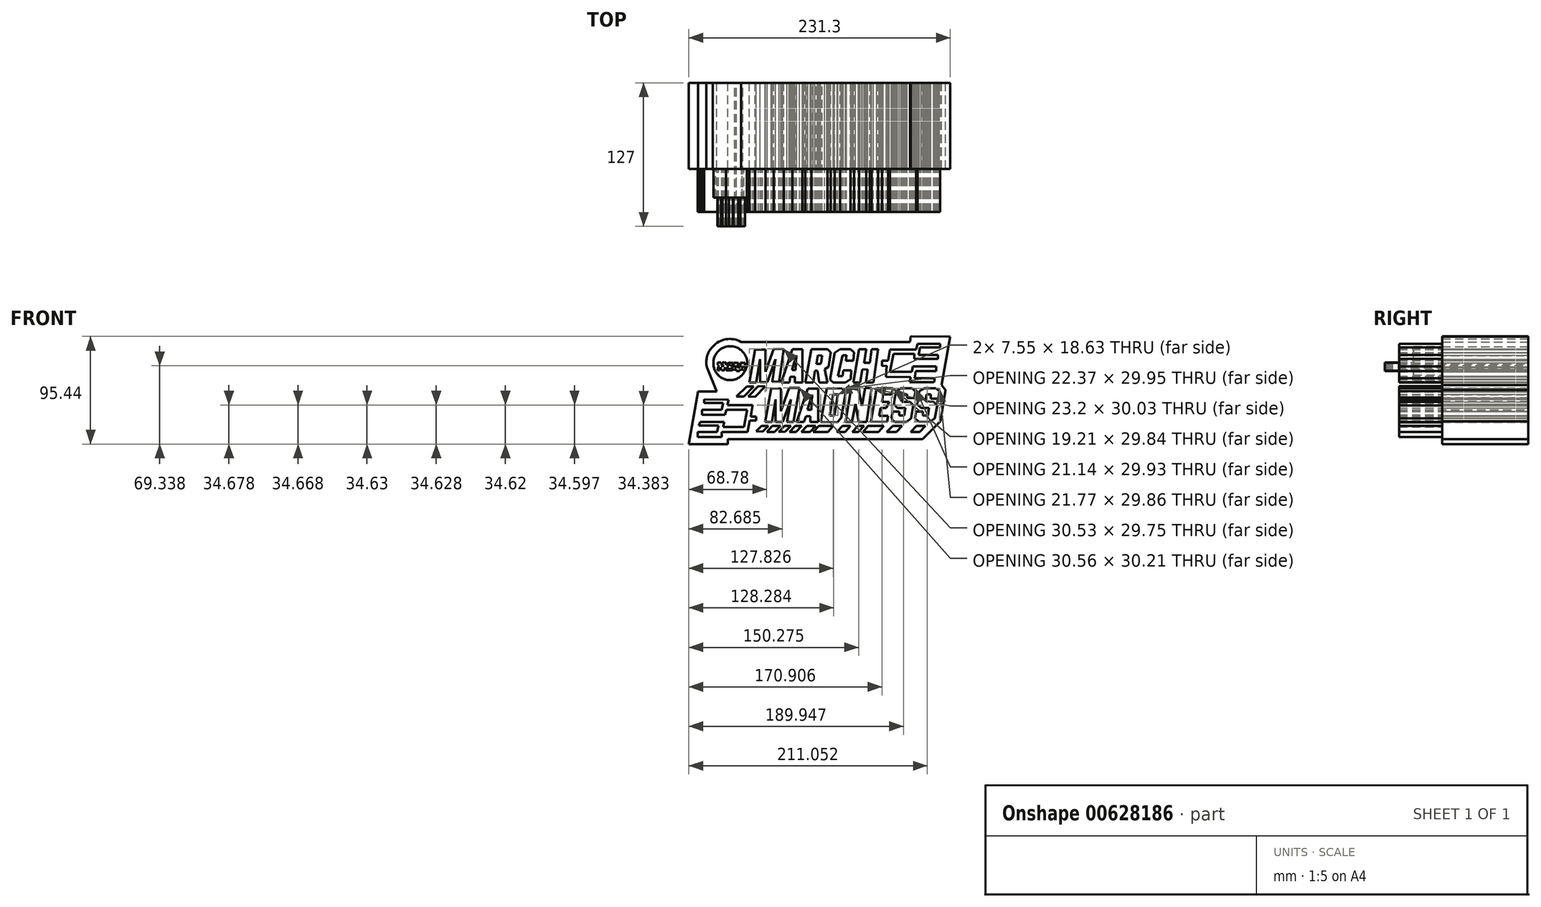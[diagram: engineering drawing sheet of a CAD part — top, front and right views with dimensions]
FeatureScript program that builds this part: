
annotation { "Feature Type Name" : "Feature", "Feature Type Description" : "" }
export const myFeature = defineFeature(function(context is Context, id is Id, definition is map)
    precondition{}
    {
        {
            var Q0;
            Q0=qCreatedBy(makeId("Front.planeOp"),FACE);
            var sketch = newSketch(context, id + "F0", { "sketchPlane" : qUnion([Q0])});
            skLineSegment(sketch, "E0", {"start": v(-36.13, -12.76) * mm, "end": v(-36.13, -15.94) * mm});
            skLineSegment(sketch, "E1", {"start": v(-36.13, -15.94) * mm, "end": v(-19.37, -15.94) * mm});
            skLineSegment(sketch, "E2", {"start": v(-19.37, -15.94) * mm, "end": v(-20.47, -21.93) * mm});
            skLineSegment(sketch, "E3", {"start": v(-20.47, -21.93) * mm, "end": v(-37.96, -21.93) * mm});
            skLineSegment(sketch, "E4", {"start": v(-37.96, -21.93) * mm, "end": v(-37.96, -26.21) * mm});
            skLineSegment(sketch, "E5", {"start": v(-37.96, -26.21) * mm, "end": v(-17.66, -26.21) * mm});
            skLineSegment(sketch, "E6", {"start": v(-17.66, -26.21) * mm, "end": v(-16.56, -21.93) * mm});
            skLineSegment(sketch, "E7", {"start": v(-16.56, -21.93) * mm, "end": v(1.79, -21.93) * mm});
            skLineSegment(sketch, "E8", {"start": v(1.79, -21.93) * mm, "end": v(-1.03, -37.22) * mm});
            skLineSegment(sketch, "E9", {"start": v(-1.03, -37.22) * mm, "end": v(-19.37, -37.22) * mm});
            skLineSegment(sketch, "E10", {"start": v(-19.37, -37.22) * mm, "end": v(-18.4, -32.82) * mm});
            skLineSegment(sketch, "E11", {"start": v(-18.4, -32.82) * mm, "end": v(-39.8, -32.82) * mm});
            skLineSegment(sketch, "E12", {"start": v(-39.8, -32.82) * mm, "end": v(-40.9, -35.88) * mm});
            skLineSegment(sketch, "E13", {"start": v(-40.9, -35.88) * mm, "end": v(-23.53, -35.88) * mm});
            skLineSegment(sketch, "E14", {"start": v(-23.53, -35.88) * mm, "end": v(-24.63, -41.62) * mm});
            skLineSegment(sketch, "E15", {"start": v(-24.63, -41.62) * mm, "end": v(-41.88, -41.62) * mm});
            skLineSegment(sketch, "E16", {"start": v(-41.88, -41.62) * mm, "end": v(-41.88, -46.15) * mm});
            skLineSegment(sketch, "E17", {"start": v(-41.88, -46.15) * mm, "end": v(-20.47, -46.15) * mm});
            skLineSegment(sketch, "E18", {"start": v(-20.47, -46.15) * mm, "end": v(-20.47, -41.62) * mm});
            skLineSegment(sketch, "E19", {"start": v(-20.47, -41.62) * mm, "end": v(2.15, -41.62) * mm});
            skLineSegment(sketch, "E20", {"start": v(2.15, -41.62) * mm, "end": v(4.23, -31.6) * mm});
            skLineSegment(sketch, "E21", {"start": v(4.23, -31.6) * mm, "end": v(9.98, -31.6) * mm});
            skLineSegment(sketch, "E22", {"start": v(9.98, -31.6) * mm, "end": v(9.98, -27.93) * mm});
            skLineSegment(sketch, "E23", {"start": v(9.98, -27.93) * mm, "end": v(5.21, -27.93) * mm});
            skLineSegment(sketch, "E24", {"start": v(5.21, -27.93) * mm, "end": v(6.68, -17.65) * mm});
            skLineSegment(sketch, "E25", {"start": v(6.68, -17.65) * mm, "end": v(-15.46, -17.65) * mm});
            skLineSegment(sketch, "E26", {"start": v(-15.46, -17.65) * mm, "end": v(-14.6, -12.88) * mm});
            skLineSegment(sketch, "E27", {"start": v(-14.6, -12.88) * mm, "end": v(-36.13, -12.76) * mm});
            skLineSegment(sketch, "E28", {"start": v(-7.5, -10.31) * mm, "end": v(1.54, -1.26) * mm});
            skLineSegment(sketch, "E29", {"start": v(1.54, -1.26) * mm, "end": v(7.54, -1.3) * mm});
            skLineSegment(sketch, "E30", {"start": v(7.54, -1.3) * mm, "end": v(-1.03, -10.31) * mm});
            skLineSegment(sketch, "E31", {"start": v(-1.03, -10.31) * mm, "end": v(-7.5, -10.31) * mm});
            skLineSegment(sketch, "E32", {"start": v(11.82, -0.9) * mm, "end": v(2.87, -10.31) * mm});
            skLineSegment(sketch, "E33", {"start": v(2.87, -10.31) * mm, "end": v(9, -10.35) * mm});
            skLineSegment(sketch, "E34", {"start": v(9, -10.35) * mm, "end": v(17.7, -1.19) * mm});
            skLineSegment(sketch, "E35", {"start": v(17.7, -1.19) * mm, "end": v(11.82, -0.9) * mm});
            skLineSegment(sketch, "E36", {"start": v(17.7, -32.82) * mm, "end": v(23.07, -2.98) * mm});
            skLineSegment(sketch, "E37", {"start": v(23.07, -2.98) * mm, "end": v(31.63, -3.02) * mm});
            skLineSegment(sketch, "E38", {"start": v(31.63, -3.02) * mm, "end": v(31.63, -23.16) * mm});
            skLineSegment(sketch, "E39", {"start": v(31.63, -23.16) * mm, "end": v(39.1, -2.6) * mm});
            skLineSegment(sketch, "E40", {"start": v(39.1, -2.6) * mm, "end": v(48.26, -2.66) * mm});
            skLineSegment(sketch, "E41", {"start": v(48.26, -2.66) * mm, "end": v(42.88, -32.82) * mm});
            skLineSegment(sketch, "E42", {"start": v(42.88, -32.82) * mm, "end": v(37.13, -32.79) * mm});
            skLineSegment(sketch, "E43", {"start": v(37.13, -32.79) * mm, "end": v(40.68, -12.76) * mm});
            skLineSegment(sketch, "E44", {"start": v(40.68, -12.76) * mm, "end": v(33.46, -32.82) * mm});
            skLineSegment(sketch, "E45", {"start": v(33.46, -32.82) * mm, "end": v(26.98, -32.78) * mm});
            skLineSegment(sketch, "E46", {"start": v(26.98, -32.78) * mm, "end": v(26.98, -12.76) * mm});
            skLineSegment(sketch, "E47", {"start": v(26.98, -12.76) * mm, "end": v(23.68, -32.82) * mm});
            skLineSegment(sketch, "E48", {"start": v(23.68, -32.82) * mm, "end": v(17.7, -32.82) * mm});
            skLineSegment(sketch, "E49", {"start": v(45.7, -32.82) * mm, "end": v(52.18, -32.85) * mm});
            skLineSegment(sketch, "E50", {"start": v(52.18, -32.85) * mm, "end": v(54.07, -27.6) * mm});
            skLineSegment(sketch, "E51", {"start": v(54.07, -27.6) * mm, "end": v(57.92, -27.62) * mm});
            skLineSegment(sketch, "E52", {"start": v(57.92, -27.62) * mm, "end": v(57.92, -32.82) * mm});
            skLineSegment(sketch, "E53", {"start": v(57.92, -32.82) * mm, "end": v(64.69, -32.86) * mm});
            skLineSegment(sketch, "E54", {"start": v(64.69, -32.86) * mm, "end": v(64.86, -3.13) * mm});
            skLineSegment(sketch, "E55", {"start": v(64.86, -3.13) * mm, "end": v(55.52, -3.08) * mm});
            skLineSegment(sketch, "E56", {"start": v(55.52, -3.08) * mm, "end": v(45.7, -32.82) * mm});
            skLineSegment(sketch, "E57", {"start": v(55.23, -21.93) * mm, "end": v(58.65, -21.95) * mm});
            skLineSegment(sketch, "E58", {"start": v(58.65, -21.95) * mm, "end": v(59.31, -8.43) * mm});
            skLineSegment(sketch, "E59", {"start": v(59.31, -8.43) * mm, "end": v(55.23, -21.93) * mm});
            skLineSegment(sketch, "E60", {"start": v(66.94, -32.82) * mm, "end": v(81.48, -32.9) * mm});
            skLineSegment(sketch, "E61", {"start": v(81.48, -32.9) * mm, "end": v(85.13, -29.25) * mm});
            skLineSegment(sketch, "E62", {"start": v(85.13, -29.25) * mm, "end": v(89.31, -6) * mm});
            skLineSegment(sketch, "E63", {"start": v(89.31, -6) * mm, "end": v(86.19, -3.03) * mm});
            skLineSegment(sketch, "E64", {"start": v(86.19, -3.03) * mm, "end": v(72.4, -2.95) * mm});
            skLineSegment(sketch, "E65", {"start": v(72.4, -2.95) * mm, "end": v(66.94, -32.82) * mm});
            skLineSegment(sketch, "E66", {"start": v(78.14, -8.37) * mm, "end": v(74.8, -26.92) * mm});
            skLineSegment(sketch, "E67", {"start": v(74.8, -26.92) * mm, "end": v(79.01, -26.95) * mm});
            skLineSegment(sketch, "E68", {"start": v(79.01, -26.95) * mm, "end": v(82.36, -8.32) * mm});
            skLineSegment(sketch, "E69", {"start": v(82.36, -8.32) * mm, "end": v(78.14, -8.37) * mm});
            skLineSegment(sketch, "E70", {"start": v(94.07, -2.77) * mm, "end": v(88.98, -32.59) * mm});
            skLineSegment(sketch, "E71", {"start": v(88.98, -32.59) * mm, "end": v(94.58, -32.62) * mm});
            skLineSegment(sketch, "E72", {"start": v(94.58, -32.62) * mm, "end": v(97.92, -16.88) * mm});
            skLineSegment(sketch, "E73", {"start": v(97.92, -16.88) * mm, "end": v(100.76, -32.66) * mm});
            skLineSegment(sketch, "E74", {"start": v(100.76, -32.66) * mm, "end": v(107.52, -32.7) * mm});
            skLineSegment(sketch, "E75", {"start": v(107.52, -32.7) * mm, "end": v(112.17, -2.7) * mm});
            skLineSegment(sketch, "E76", {"start": v(112.17, -2.7) * mm, "end": v(106.43, -2.67) * mm});
            skLineSegment(sketch, "E77", {"start": v(106.43, -2.67) * mm, "end": v(103.67, -18.4) * mm});
            skLineSegment(sketch, "E78", {"start": v(103.67, -18.4) * mm, "end": v(100.4, -2.99) * mm});
            skLineSegment(sketch, "E79", {"start": v(100.4, -2.99) * mm, "end": v(94.07, -2.77) * mm});
            skLineSegment(sketch, "E80", {"start": v(116.68, -2.77) * mm, "end": v(111.6, -32.53) * mm});
            skLineSegment(sketch, "E81", {"start": v(111.6, -32.53) * mm, "end": v(125.7, -32.61) * mm});
            skLineSegment(sketch, "E82", {"start": v(125.7, -32.61) * mm, "end": v(126.6, -27.3) * mm});
            skLineSegment(sketch, "E83", {"start": v(126.6, -27.3) * mm, "end": v(118.86, -27.26) * mm});
            skLineSegment(sketch, "E84", {"start": v(118.86, -27.26) * mm, "end": v(120.06, -20.24) * mm});
            skLineSegment(sketch, "E85", {"start": v(120.06, -20.24) * mm, "end": v(125.26, -20.27) * mm});
            skLineSegment(sketch, "E86", {"start": v(125.26, -20.27) * mm, "end": v(127.52, -14.99) * mm});
            skLineSegment(sketch, "E87", {"start": v(127.52, -14.99) * mm, "end": v(121.26, -14.95) * mm});
            skLineSegment(sketch, "E88", {"start": v(121.26, -14.95) * mm, "end": v(122.39, -8.37) * mm});
            skLineSegment(sketch, "E89", {"start": v(122.39, -8.37) * mm, "end": v(129.85, -8.41) * mm});
            skLineSegment(sketch, "E90", {"start": v(129.85, -8.41) * mm, "end": v(130.8, -2.77) * mm});
            skLineSegment(sketch, "E91", {"start": v(130.8, -2.77) * mm, "end": v(116.68, -2.77) * mm});
            skLineSegment(sketch, "E92", {"start": v(133.63, -5.53) * mm, "end": v(131.7, -16.82) * mm});
            skLineSegment(sketch, "E93", {"start": v(131.7, -16.82) * mm, "end": v(134.8, -20.22) * mm});
            skLineSegment(sketch, "E94", {"start": v(134.8, -20.22) * mm, "end": v(142.06, -20.27) * mm});
            skLineSegment(sketch, "E95", {"start": v(142.06, -20.27) * mm, "end": v(140.9, -27.12) * mm});
            skLineSegment(sketch, "E96", {"start": v(140.9, -27.12) * mm, "end": v(136.54, -27.1) * mm});
            skLineSegment(sketch, "E97", {"start": v(136.54, -27.1) * mm, "end": v(136.54, -23.57) * mm});
            skLineSegment(sketch, "E98", {"start": v(136.54, -23.57) * mm, "end": v(130.72, -23.54) * mm});
            skLineSegment(sketch, "E99", {"start": v(130.72, -23.54) * mm, "end": v(129.68, -29.63) * mm});
            skLineSegment(sketch, "E100", {"start": v(129.68, -29.63) * mm, "end": v(132.4, -32.59) * mm});
            skLineSegment(sketch, "E101", {"start": v(132.4, -32.59) * mm, "end": v(142.8, -32.65) * mm});
            skLineSegment(sketch, "E102", {"start": v(142.8, -32.65) * mm, "end": v(146.94, -29.39) * mm});
            skLineSegment(sketch, "E103", {"start": v(146.94, -29.39) * mm, "end": v(148.89, -17.94) * mm});
            skLineSegment(sketch, "E104", {"start": v(148.89, -17.94) * mm, "end": v(146.06, -14.84) * mm});
            skLineSegment(sketch, "E105", {"start": v(146.06, -14.84) * mm, "end": v(138.8, -14.8) * mm});
            skLineSegment(sketch, "E106", {"start": v(138.8, -14.8) * mm, "end": v(139.89, -8.37) * mm});
            skLineSegment(sketch, "E107", {"start": v(139.89, -8.37) * mm, "end": v(143.66, -8.4) * mm});
            skLineSegment(sketch, "E108", {"start": v(143.66, -8.4) * mm, "end": v(143.66, -11.5) * mm});
            skLineSegment(sketch, "E109", {"start": v(143.66, -11.5) * mm, "end": v(149.84, -11.53) * mm});
            skLineSegment(sketch, "E110", {"start": v(149.84, -11.53) * mm, "end": v(150.82, -5.84) * mm});
            skLineSegment(sketch, "E111", {"start": v(150.82, -5.84) * mm, "end": v(147.88, -2.77) * mm});
            skLineSegment(sketch, "E112", {"start": v(147.88, -2.77) * mm, "end": v(138, -2.71) * mm});
            skLineSegment(sketch, "E113", {"start": v(138, -2.71) * mm, "end": v(133.63, -5.53) * mm});
            skLineSegment(sketch, "E114", {"start": v(159.8, -14.33) * mm, "end": v(160.83, -8.37) * mm});
            skLineSegment(sketch, "E115", {"start": v(160.83, -8.37) * mm, "end": v(164.53, -8.4) * mm});
            skLineSegment(sketch, "E116", {"start": v(164.53, -8.4) * mm, "end": v(164.53, -11.93) * mm});
            skLineSegment(sketch, "E117", {"start": v(164.53, -11.93) * mm, "end": v(170.13, -11.97) * mm});
            skLineSegment(sketch, "E118", {"start": v(170.13, -11.97) * mm, "end": v(171.26, -11.24) * mm});
            skLineSegment(sketch, "E119", {"start": v(171.26, -11.24) * mm, "end": v(172.24, -5.53) * mm});
            skLineSegment(sketch, "E120", {"start": v(172.24, -5.53) * mm, "end": v(168.97, -2.77) * mm});
            skLineSegment(sketch, "E121", {"start": v(168.97, -2.77) * mm, "end": v(158.72, -2.71) * mm});
            skLineSegment(sketch, "E122", {"start": v(158.72, -2.71) * mm, "end": v(154.35, -5.53) * mm});
            skLineSegment(sketch, "E123", {"start": v(154.35, -5.53) * mm, "end": v(152.35, -17.26) * mm});
            skLineSegment(sketch, "E124", {"start": v(152.35, -17.26) * mm, "end": v(155.8, -20.22) * mm});
            skLineSegment(sketch, "E125", {"start": v(155.8, -20.22) * mm, "end": v(162.93, -20.26) * mm});
            skLineSegment(sketch, "E126", {"start": v(162.93, -20.26) * mm, "end": v(161.79, -26.99) * mm});
            skLineSegment(sketch, "E127", {"start": v(161.79, -26.99) * mm, "end": v(157.55, -26.97) * mm});
            skLineSegment(sketch, "E128", {"start": v(157.55, -26.97) * mm, "end": v(157.55, -23.57) * mm});
            skLineSegment(sketch, "E129", {"start": v(157.55, -23.57) * mm, "end": v(151.52, -23.53) * mm});
            skLineSegment(sketch, "E130", {"start": v(151.52, -23.53) * mm, "end": v(150.47, -29.67) * mm});
            skLineSegment(sketch, "E131", {"start": v(150.47, -29.67) * mm, "end": v(153.55, -32.51) * mm});
            skLineSegment(sketch, "E132", {"start": v(153.55, -32.51) * mm, "end": v(163.59, -32.57) * mm});
            skLineSegment(sketch, "E133", {"start": v(163.59, -32.57) * mm, "end": v(168.1, -29.65) * mm});
            skLineSegment(sketch, "E134", {"start": v(168.1, -29.65) * mm, "end": v(170.1, -18.02) * mm});
            skLineSegment(sketch, "E135", {"start": v(170.1, -18.02) * mm, "end": v(167, -14.84) * mm});
            skLineSegment(sketch, "E136", {"start": v(167, -14.84) * mm, "end": v(159.8, -14.33) * mm});
            skLineSegment(sketch, "E137", {"start": v(14.47, -36.25) * mm, "end": v(9.76, -41.02) * mm});
            skLineSegment(sketch, "E138", {"start": v(9.76, -41.02) * mm, "end": v(15.57, -41.44) * mm});
            skLineSegment(sketch, "E139", {"start": v(15.57, -41.44) * mm, "end": v(20.7, -36.25) * mm});
            skLineSegment(sketch, "E140", {"start": v(20.7, -36.25) * mm, "end": v(14.47, -36.25) * mm});
            skLineSegment(sketch, "E141", {"start": v(24.19, -36.25) * mm, "end": v(19.3, -41.45) * mm});
            skLineSegment(sketch, "E142", {"start": v(19.3, -41.45) * mm, "end": v(26.08, -41.5) * mm});
            skLineSegment(sketch, "E143", {"start": v(26.08, -41.5) * mm, "end": v(31.34, -36.25) * mm});
            skLineSegment(sketch, "E144", {"start": v(31.34, -36.25) * mm, "end": v(24.19, -36.25) * mm});
            skLineSegment(sketch, "E145", {"start": v(29.94, -41.45) * mm, "end": v(34.83, -36.25) * mm});
            skLineSegment(sketch, "E146", {"start": v(34.83, -36.25) * mm, "end": v(40.64, -36.29) * mm});
            skLineSegment(sketch, "E147", {"start": v(40.64, -36.29) * mm, "end": v(35.56, -41.4) * mm});
            skLineSegment(sketch, "E148", {"start": v(35.56, -41.4) * mm, "end": v(29.94, -41.45) * mm});
            skLineSegment(sketch, "E149", {"start": v(39.23, -41.45) * mm, "end": v(44.3, -36.25) * mm});
            skLineSegment(sketch, "E150", {"start": v(44.3, -36.25) * mm, "end": v(50.24, -36.29) * mm});
            skLineSegment(sketch, "E151", {"start": v(50.24, -36.29) * mm, "end": v(45.22, -41.45) * mm});
            skLineSegment(sketch, "E152", {"start": v(45.22, -41.45) * mm, "end": v(39.23, -41.45) * mm});
            skLineSegment(sketch, "E153", {"start": v(49.75, -41.45) * mm, "end": v(55, -36.25) * mm});
            skLineSegment(sketch, "E154", {"start": v(55, -36.25) * mm, "end": v(62.6, -36.3) * mm});
            skLineSegment(sketch, "E155", {"start": v(62.6, -36.3) * mm, "end": v(57.58, -41.45) * mm});
            skLineSegment(sketch, "E156", {"start": v(57.58, -41.45) * mm, "end": v(49.75, -41.45) * mm});
            skLineSegment(sketch, "E157", {"start": v(60.51, -41.45) * mm, "end": v(65.47, -36.25) * mm});
            skLineSegment(sketch, "E158", {"start": v(65.47, -36.25) * mm, "end": v(78.14, -36.33) * mm});
            skLineSegment(sketch, "E159", {"start": v(78.14, -36.33) * mm, "end": v(73.48, -41.45) * mm});
            skLineSegment(sketch, "E160", {"start": v(73.48, -41.45) * mm, "end": v(60.51, -41.45) * mm});
            skLineSegment(sketch, "E161", {"start": v(81.3, -41.45) * mm, "end": v(86.5, -36.25) * mm});
            skLineSegment(sketch, "E162", {"start": v(86.5, -36.25) * mm, "end": v(93.47, -36.3) * mm});
            skLineSegment(sketch, "E163", {"start": v(93.47, -36.3) * mm, "end": v(88.46, -41.45) * mm});
            skLineSegment(sketch, "E164", {"start": v(88.46, -41.45) * mm, "end": v(81.3, -41.45) * mm});
            skLineSegment(sketch, "E165", {"start": v(94.82, -41.45) * mm, "end": v(99.96, -36.25) * mm});
            skLineSegment(sketch, "E166", {"start": v(99.96, -36.25) * mm, "end": v(105.46, -36.25) * mm});
            skLineSegment(sketch, "E167", {"start": v(105.46, -36.25) * mm, "end": v(100.45, -41.45) * mm});
            skLineSegment(sketch, "E168", {"start": v(100.45, -41.45) * mm, "end": v(94.82, -41.45) * mm});
            skLineSegment(sketch, "E169", {"start": v(104.48, -41.45) * mm, "end": v(109.07, -36.25) * mm});
            skLineSegment(sketch, "E170", {"start": v(109.07, -36.25) * mm, "end": v(123, -36.33) * mm});
            skLineSegment(sketch, "E171", {"start": v(123, -36.33) * mm, "end": v(118.18, -41.45) * mm});
            skLineSegment(sketch, "E172", {"start": v(118.18, -41.45) * mm, "end": v(104.48, -41.45) * mm});
            skLineSegment(sketch, "E173", {"start": v(125.46, -41.45) * mm, "end": v(130.72, -36.25) * mm});
            skLineSegment(sketch, "E174", {"start": v(130.72, -36.25) * mm, "end": v(139.1, -36.3) * mm});
            skLineSegment(sketch, "E175", {"start": v(139.1, -36.3) * mm, "end": v(134.14, -41.45) * mm});
            skLineSegment(sketch, "E176", {"start": v(134.14, -41.45) * mm, "end": v(125.46, -41.45) * mm});
            skLineSegment(sketch, "E177", {"start": v(146.74, -41.45) * mm, "end": v(151.7, -36.25) * mm});
            skLineSegment(sketch, "E178", {"start": v(151.7, -36.25) * mm, "end": v(159.8, -36.3) * mm});
            skLineSegment(sketch, "E179", {"start": v(159.8, -36.3) * mm, "end": v(154.75, -41.45) * mm});
            skLineSegment(sketch, "E180", {"start": v(154.75, -41.45) * mm, "end": v(146.74, -41.45) * mm});
            skLineSegment(sketch, "E181", {"start": v(3.82, 2.17) * mm, "end": v(9, 31.46) * mm});
            skLineSegment(sketch, "E182", {"start": v(9, 31.46) * mm, "end": v(18.26, 31.4) * mm});
            skLineSegment(sketch, "E183", {"start": v(18.26, 31.4) * mm, "end": v(18.17, 11.77) * mm});
            skLineSegment(sketch, "E184", {"start": v(18.17, 11.77) * mm, "end": v(25.48, 31.9) * mm});
            skLineSegment(sketch, "E185", {"start": v(25.48, 31.9) * mm, "end": v(34.34, 31.85) * mm});
            skLineSegment(sketch, "E186", {"start": v(34.34, 31.85) * mm, "end": v(30.18, 2.7) * mm});
            skLineSegment(sketch, "E187", {"start": v(30.18, 2.7) * mm, "end": v(24.19, 2.74) * mm});
            skLineSegment(sketch, "E188", {"start": v(24.19, 2.74) * mm, "end": v(27.04, 22.7) * mm});
            skLineSegment(sketch, "E189", {"start": v(27.04, 22.7) * mm, "end": v(19.74, 2.6) * mm});
            skLineSegment(sketch, "E190", {"start": v(19.74, 2.6) * mm, "end": v(13.5, 2.64) * mm});
            skLineSegment(sketch, "E191", {"start": v(13.5, 2.64) * mm, "end": v(13.5, 22.75) * mm});
            skLineSegment(sketch, "E192", {"start": v(13.5, 22.75) * mm, "end": v(9.98, 2.15) * mm});
            skLineSegment(sketch, "E193", {"start": v(9.98, 2.15) * mm, "end": v(3.82, 2.17) * mm});
            skLineSegment(sketch, "E194", {"start": v(32.1, 2.17) * mm, "end": v(41.78, 31.75) * mm});
            skLineSegment(sketch, "E195", {"start": v(41.78, 31.75) * mm, "end": v(50.69, 31.7) * mm});
            skLineSegment(sketch, "E196", {"start": v(50.69, 31.7) * mm, "end": v(50.69, 2.17) * mm});
            skLineSegment(sketch, "E197", {"start": v(50.69, 2.17) * mm, "end": v(44.29, 2.2) * mm});
            skLineSegment(sketch, "E198", {"start": v(44.29, 2.2) * mm, "end": v(44.29, 7.27) * mm});
            skLineSegment(sketch, "E199", {"start": v(44.29, 7.27) * mm, "end": v(40.14, 7.3) * mm});
            skLineSegment(sketch, "E200", {"start": v(40.14, 7.3) * mm, "end": v(39.26, 2.17) * mm});
            skLineSegment(sketch, "E201", {"start": v(39.26, 2.17) * mm, "end": v(32.1, 2.17) * mm});
            skLineSegment(sketch, "E202", {"start": v(53.37, 2.17) * mm, "end": v(58.6, 31.7) * mm});
            skLineSegment(sketch, "E203", {"start": v(58.6, 31.7) * mm, "end": v(72.91, 31.62) * mm});
            skLineSegment(sketch, "E204", {"start": v(72.91, 31.62) * mm, "end": v(75.82, 28.86) * mm});
            skLineSegment(sketch, "E205", {"start": v(75.82, 28.86) * mm, "end": v(74.02, 16.32) * mm});
            skLineSegment(sketch, "E206", {"start": v(74.02, 16.32) * mm, "end": v(70.56, 14.08) * mm});
            skLineSegment(sketch, "E207", {"start": v(70.56, 14.08) * mm, "end": v(72.92, 2.17) * mm});
            skLineSegment(sketch, "E208", {"start": v(72.92, 2.17) * mm, "end": v(65.74, 2.21) * mm});
            skLineSegment(sketch, "E209", {"start": v(65.74, 2.21) * mm, "end": v(64.18, 12.55) * mm});
            skLineSegment(sketch, "E210", {"start": v(64.18, 12.55) * mm, "end": v(61.85, 12.56) * mm});
            skLineSegment(sketch, "E211", {"start": v(61.85, 12.56) * mm, "end": v(60.36, 2.17) * mm});
            skLineSegment(sketch, "E212", {"start": v(60.36, 2.17) * mm, "end": v(53.37, 2.17) * mm});
            skLineSegment(sketch, "E213", {"start": v(89.09, 21.54) * mm, "end": v(89.78, 26.37) * mm});
            skLineSegment(sketch, "E214", {"start": v(89.78, 26.37) * mm, "end": v(86.23, 26.4) * mm});
            skLineSegment(sketch, "E215", {"start": v(86.23, 26.4) * mm, "end": v(82.36, 7.96) * mm});
            skLineSegment(sketch, "E216", {"start": v(82.36, 7.96) * mm, "end": v(86.23, 7.94) * mm});
            skLineSegment(sketch, "E217", {"start": v(86.23, 7.94) * mm, "end": v(86.95, 12.95) * mm});
            skLineSegment(sketch, "E218", {"start": v(86.95, 12.95) * mm, "end": v(94.07, 12.91) * mm});
            skLineSegment(sketch, "E219", {"start": v(94.07, 12.91) * mm, "end": v(93.52, 5.24) * mm});
            skLineSegment(sketch, "E220", {"start": v(93.52, 5.24) * mm, "end": v(88.77, 2.17) * mm});
            skLineSegment(sketch, "E221", {"start": v(88.77, 2.17) * mm, "end": v(78.14, 2.17) * mm});
            skLineSegment(sketch, "E222", {"start": v(78.14, 2.17) * mm, "end": v(75.33, 4.84) * mm});
            skLineSegment(sketch, "E223", {"start": v(75.33, 4.84) * mm, "end": v(79.4, 28.68) * mm});
            skLineSegment(sketch, "E224", {"start": v(79.4, 28.68) * mm, "end": v(84.07, 31.7) * mm});
            skLineSegment(sketch, "E225", {"start": v(84.07, 31.7) * mm, "end": v(93.32, 31.64) * mm});
            skLineSegment(sketch, "E226", {"start": v(93.32, 31.64) * mm, "end": v(96.38, 28.74) * mm});
            skLineSegment(sketch, "E227", {"start": v(96.38, 28.74) * mm, "end": v(95.87, 21.6) * mm});
            skLineSegment(sketch, "E228", {"start": v(95.87, 21.6) * mm, "end": v(89.09, 21.54) * mm});
            skLineSegment(sketch, "E229", {"start": v(107.34, 31.7) * mm, "end": v(101.02, 31.73) * mm});
            skLineSegment(sketch, "E230", {"start": v(101.02, 31.73) * mm, "end": v(95.97, 2.17) * mm});
            skLineSegment(sketch, "E231", {"start": v(95.97, 2.17) * mm, "end": v(101.89, 2.14) * mm});
            skLineSegment(sketch, "E232", {"start": v(101.89, 2.14) * mm, "end": v(103.88, 13.82) * mm});
            skLineSegment(sketch, "E233", {"start": v(103.88, 13.82) * mm, "end": v(108.72, 13.79) * mm});
            skLineSegment(sketch, "E234", {"start": v(108.72, 13.79) * mm, "end": v(107.06, 2.17) * mm});
            skLineSegment(sketch, "E235", {"start": v(107.06, 2.17) * mm, "end": v(113.65, 2.17) * mm});
            skLineSegment(sketch, "E236", {"start": v(113.65, 2.17) * mm, "end": v(117.87, 31.7) * mm});
            skLineSegment(sketch, "E237", {"start": v(117.87, 31.7) * mm, "end": v(112.18, 31.75) * mm});
            skLineSegment(sketch, "E238", {"start": v(112.18, 31.75) * mm, "end": v(110.45, 19.66) * mm});
            skLineSegment(sketch, "E239", {"start": v(110.45, 19.66) * mm, "end": v(105.52, 19.7) * mm});
            skLineSegment(sketch, "E240", {"start": v(105.52, 19.7) * mm, "end": v(107.34, 31.7) * mm});
            skLineSegment(sketch, "E241", {"start": v(121.26, 21.54) * mm, "end": v(121.26, 16.96) * mm});
            skPoint(sketch, "E241.endSnap0", {"position": v(36.94, 16.96) * mm});
            skLineSegment(sketch, "E242", {"start": v(121.26, 16.96) * mm, "end": v(125.46, 17.26) * mm});
            skLineSegment(sketch, "E243", {"start": v(125.46, 17.26) * mm, "end": v(124.74, 7.14) * mm});
            skLineSegment(sketch, "E244", {"start": v(124.74, 7.14) * mm, "end": v(146.74, 7.02) * mm});
            skLineSegment(sketch, "E245", {"start": v(146.74, 7.02) * mm, "end": v(145.8, 2.55) * mm});
            skLineSegment(sketch, "E246", {"start": v(145.8, 2.55) * mm, "end": v(167.19, 2.55) * mm});
            skLineSegment(sketch, "E247", {"start": v(167.19, 2.55) * mm, "end": v(167.9, 6.05) * mm});
            skLineSegment(sketch, "E248", {"start": v(167.9, 6.05) * mm, "end": v(150.32, 6.05) * mm});
            skLineSegment(sketch, "E249", {"start": v(150.32, 6.05) * mm, "end": v(151.25, 12.53) * mm});
            skLineSegment(sketch, "E250", {"start": v(151.25, 12.53) * mm, "end": v(169.24, 12.53) * mm});
            skLineSegment(sketch, "E251", {"start": v(169.24, 12.53) * mm, "end": v(169.24, 16.54) * mm});
            skLineSegment(sketch, "E252", {"start": v(169.24, 16.54) * mm, "end": v(148.47, 16.54) * mm});
            skLineSegment(sketch, "E253", {"start": v(148.47, 16.54) * mm, "end": v(147.54, 11.7) * mm});
            skLineSegment(sketch, "E254", {"start": v(147.54, 11.7) * mm, "end": v(128.41, 11.7) * mm});
            skLineSegment(sketch, "E255", {"start": v(128.41, 11.7) * mm, "end": v(131.5, 27.65) * mm});
            skLineSegment(sketch, "E256", {"start": v(131.5, 27.65) * mm, "end": v(150.01, 27.65) * mm});
            skLineSegment(sketch, "E257", {"start": v(150.01, 27.65) * mm, "end": v(150.01, 23.12) * mm});
            skLineSegment(sketch, "E258", {"start": v(150.01, 23.12) * mm, "end": v(170.89, 23.12) * mm});
            skLineSegment(sketch, "E259", {"start": v(170.89, 23.12) * mm, "end": v(170.89, 26.62) * mm});
            skLineSegment(sketch, "E260", {"start": v(170.89, 26.62) * mm, "end": v(153.82, 26.62) * mm});
            skLineSegment(sketch, "E261", {"start": v(153.82, 26.62) * mm, "end": v(155.05, 33.2) * mm});
            skLineSegment(sketch, "E262", {"start": v(155.05, 33.2) * mm, "end": v(172.84, 33.2) * mm});
            skLineSegment(sketch, "E263", {"start": v(172.84, 33.2) * mm, "end": v(172.84, 36.6) * mm});
            skLineSegment(sketch, "E264", {"start": v(172.84, 36.6) * mm, "end": v(152.68, 36.6) * mm});
            skLineSegment(sketch, "E265", {"start": v(152.68, 36.6) * mm, "end": v(151.45, 31.35) * mm});
            skLineSegment(sketch, "E266", {"start": v(151.45, 31.35) * mm, "end": v(128.41, 31.35) * mm});
            skLineSegment(sketch, "E267", {"start": v(128.41, 31.35) * mm, "end": v(126.67, 21.68) * mm});
            skLineSegment(sketch, "E268", {"start": v(126.67, 21.68) * mm, "end": v(121.26, 21.54) * mm});
            skLineSegment(sketch, "E269", {"start": v(-23.28, 17.85) * mm, "end": v(-24.01, 17.85) * mm});
            skLineSegment(sketch, "E270", {"start": v(-24.01, 17.85) * mm, "end": v(-24, 19.84) * mm});
            skLineSegment(sketch, "E271", {"start": v(-24, 19.84) * mm, "end": v(-21.33, 19.84) * mm});
            skLineSegment(sketch, "E272", {"start": v(-21.33, 19.84) * mm, "end": v(-19.6, 15.77) * mm});
            skLineSegment(sketch, "E273", {"start": v(-19.6, 15.77) * mm, "end": v(-19.25, 17.76) * mm});
            skLineSegment(sketch, "E274", {"start": v(-19.25, 17.76) * mm, "end": v(-19.95, 17.76) * mm});
            skLineSegment(sketch, "E275", {"start": v(-19.95, 17.76) * mm, "end": v(-19.95, 20.01) * mm});
            skLineSegment(sketch, "E276", {"start": v(-19.95, 20.01) * mm, "end": v(-16.83, 20.01) * mm});
            skLineSegment(sketch, "E277", {"start": v(-16.83, 20.01) * mm, "end": v(-16.83, 17.63) * mm});
            skLineSegment(sketch, "E278", {"start": v(-24.45, 12.88) * mm, "end": v(-23.28, 17.85) * mm});
            skLineSegment(sketch, "E279", {"start": v(-24.45, 12.88) * mm, "end": v(-22.59, 12.88) * mm});
            skLineSegment(sketch, "E280", {"start": v(-22.59, 12.88) * mm, "end": v(-22.11, 15.95) * mm});
            skLineSegment(sketch, "E281", {"start": v(-22.11, 15.95) * mm, "end": v(-20.51, 12.88) * mm});
            skLineSegment(sketch, "E282", {"start": v(-20.51, 12.88) * mm, "end": v(-18.13, 12.88) * mm});
            skLineSegment(sketch, "E283", {"start": v(-18.13, 12.88) * mm, "end": v(-18.13, 14.43) * mm});
            skLineSegment(sketch, "E284", {"start": v(-13.03, 18.02) * mm, "end": v(-13.03, 17.07) * mm});
            skLineSegment(sketch, "E285", {"start": v(-13.03, 17.07) * mm, "end": v(-10.82, 17.07) * mm});
            skLineSegment(sketch, "E286", {"start": v(-10.82, 17.07) * mm, "end": v(-10.82, 19.67) * mm});
            skLineSegment(sketch, "E287", {"start": v(-10.82, 19.67) * mm, "end": v(-14.41, 19.67) * mm});
            skLineSegment(sketch, "E288", {"start": v(-16.06, 12.88) * mm, "end": v(-10.95, 12.88) * mm});
            skLineSegment(sketch, "E289", {"start": v(-14.72, 14.17) * mm, "end": v(-11.9, 14.17) * mm});
            skLineSegment(sketch, "E290", {"start": v(-11.9, 14.17) * mm, "end": v(-9.48, 17.72) * mm});
            skLineSegment(sketch, "E291", {"start": v(-9.48, 17.72) * mm, "end": v(-10.05, 18.1) * mm});
            skLineSegment(sketch, "E292", {"start": v(-10.05, 18.1) * mm, "end": v(-10.05, 19.58) * mm});
            skLineSegment(sketch, "E293", {"start": v(-10.05, 19.58) * mm, "end": v(-5.9, 19.58) * mm});
            skLineSegment(sketch, "E294", {"start": v(-5.9, 19.58) * mm, "end": v(-5.9, 14.95) * mm});
            skLineSegment(sketch, "E295", {"start": v(-5.9, 14.95) * mm, "end": v(-3.39, 17.85) * mm});
            skLineSegment(sketch, "E296", {"start": v(-3.39, 17.85) * mm, "end": v(-4.25, 17.85) * mm});
            skLineSegment(sketch, "E297", {"start": v(-4.25, 17.85) * mm, "end": v(-4.25, 19.67) * mm});
            skLineSegment(sketch, "E298", {"start": v(-4.25, 19.67) * mm, "end": v(0, 19.67) * mm});
            skLineSegment(sketch, "E299", {"start": v(0, 19.67) * mm, "end": v(0, 12.66) * mm});
            skLineSegment(sketch, "E300", {"start": v(0, 12.66) * mm, "end": v(-1.57, 12.66) * mm});
            skLineSegment(sketch, "E301", {"start": v(-1.57, 12.66) * mm, "end": v(-1.57, 13.61) * mm});
            skLineSegment(sketch, "E302", {"start": v(-1.57, 13.61) * mm, "end": v(-4.68, 13.61) * mm});
            skLineSegment(sketch, "E303", {"start": v(-4.68, 13.61) * mm, "end": v(-4.68, 12.44) * mm});
            skLineSegment(sketch, "E304", {"start": v(-4.68, 12.44) * mm, "end": v(-7.62, 12.44) * mm});
            skLineSegment(sketch, "E305", {"start": v(-7.62, 12.44) * mm, "end": v(-7.62, 13.52) * mm});
            skLineSegment(sketch, "E306", {"start": v(-7.62, 13.52) * mm, "end": v(-10.95, 13.52) * mm});
            skLineSegment(sketch, "E307", {"start": v(-10.95, 13.52) * mm, "end": v(-10.95, 12.88) * mm});
            skLineSegment(sketch, "E308", {"start": v(-8.14, 17.5) * mm, "end": v(-9.22, 15.25) * mm});
            skLineSegment(sketch, "E309", {"start": v(-9.22, 15.25) * mm, "end": v(-7.71, 15.25) * mm});
            skLineSegment(sketch, "E310", {"start": v(-7.71, 15.25) * mm, "end": v(-8.14, 17.5) * mm});
            skLineSegment(sketch, "E311", {"start": v(-1.96, 17.5) * mm, "end": v(-3.3, 15.17) * mm});
            skLineSegment(sketch, "E312", {"start": v(-3.3, 15.17) * mm, "end": v(-1.92, 15.17) * mm});
            skLineSegment(sketch, "E313", {"start": v(-1.92, 15.17) * mm, "end": v(-1.96, 17.5) * mm});
            skArc(sketch, "E314", {"start": v(-14.41, 19.67) * mm, "mid": v(-15.73, 18.78) * mm, "end": v(-16.83, 17.63) * mm});
            skArc(sketch, "E315", {"start": v(-13.03, 18.02) * mm, "mid": v(-15.22, 16.69) * mm, "end": v(-14.72, 14.17) * mm});
            skArc(sketch, "E316", {"start": v(-17.35, 15.47) * mm, "mid": v(-17.07, 13.99) * mm, "end": v(-16.06, 12.88) * mm});
            skArc(sketch, "E317", {"start": v(-16.83, 34) * mm, "mid": v(-26.9, 25.19) * mm, "end": v(-26.04, 11.83) * mm});
            skArc(sketch, "E318", {"start": v(1.57, 23.35) * mm, "mid": v(-5.53, 32.3) * mm, "end": v(-16.83, 34) * mm});
            skArc(sketch, "E319", {"start": v(-26.04, 11.83) * mm, "mid": v(-14.99, 4.4) * mm, "end": v(-2.49, 9) * mm});
            skArc(sketch, "E320", {"start": v(-2.49, 9) * mm, "mid": v(1.34, 15.67) * mm, "end": v(1.57, 23.35) * mm});
            skArc(sketch, "E321", {"start": v(-3.52, 38.2) * mm, "mid": v(-16.77, 40.56) * mm, "end": v(-28.51, 34) * mm});
            skArc(sketch, "E322", {"start": v(-28.51, 34) * mm, "mid": v(-33.58, 25.43) * mm, "end": v(-33.65, 15.47) * mm});
            skLineSegment(sketch, "E323", {"start": v(-25.22, -5.62) * mm, "end": v(-33.65, 15.47) * mm});
            skLineSegment(sketch, "E324", {"start": v(-25.22, -5.62) * mm, "end": v(-41.68, -5.62) * mm});
            skLineSegment(sketch, "E325", {"start": v(-41.68, -5.62) * mm, "end": v(-49.7, -52.3) * mm});
            skLineSegment(sketch, "E326", {"start": v(-49.7, -52.3) * mm, "end": v(-15.24, -52.3) * mm});
            skLineSegment(sketch, "E327", {"start": v(-15.24, -52.3) * mm, "end": v(-15.24, -47.99) * mm});
            skLineSegment(sketch, "E328", {"start": v(-15.24, -47.99) * mm, "end": v(157.12, -47.99) * mm});
            skLineSegment(sketch, "E329", {"start": v(157.12, -47.99) * mm, "end": v(173.07, -32.05) * mm});
            skLineSegment(sketch, "E330", {"start": v(173.07, -32.05) * mm, "end": v(177.6, -4.59) * mm});
            skLineSegment(sketch, "E331", {"start": v(177.6, -4.59) * mm, "end": v(173.89, 0) * mm});
            skLineSegment(sketch, "E332", {"start": v(173.89, 0) * mm, "end": v(181.6, 42.93) * mm});
            skLineSegment(sketch, "E333", {"start": v(181.6, 42.93) * mm, "end": v(146.63, 43.13) * mm});
            skLineSegment(sketch, "E334", {"start": v(146.63, 43.13) * mm, "end": v(146.02, 38.2) * mm});
            skLineSegment(sketch, "E335", {"start": v(146.02, 38.2) * mm, "end": v(-3.52, 38.2) * mm});
            skLineSegment(sketch, "E336", {"start": v(45.46, 26.34) * mm, "end": v(41.65, 13.19) * mm});
            skLineSegment(sketch, "E337", {"start": v(41.65, 13.19) * mm, "end": v(44.74, 13.19) * mm});
            skLineSegment(sketch, "E338", {"start": v(44.74, 13.19) * mm, "end": v(45.46, 26.34) * mm});
            skLineSegment(sketch, "E339", {"start": v(64.43, 26.34) * mm, "end": v(63.21, 18.65) * mm});
            skLineSegment(sketch, "E340", {"start": v(63.21, 18.65) * mm, "end": v(66.66, 18.65) * mm});
            skLineSegment(sketch, "E341", {"start": v(66.66, 18.65) * mm, "end": v(67.43, 19.28) * mm});
            skLineSegment(sketch, "E342", {"start": v(67.43, 19.28) * mm, "end": v(68.37, 26.09) * mm});
            skLineSegment(sketch, "E343", {"start": v(68.37, 26.09) * mm, "end": v(64.43, 26.34) * mm});
            skArc(sketch, "E344", {"start": v(-17.35, 15.47) * mm, "mid": v(-17.92, 15.08) * mm, "end": v(-18.13, 14.43) * mm});
            skSolve(sketch);
        }
        {
            var Q0;
            Q0=makeQuery(id+"F0.imprint","IMPRINT",FACE,{"disambiguationData":[TD([[makeQuery(id+"F0.imprint","IMPRINT",EDGE,{"derivedFrom":sQuery(id+"F0.wireOp",EDGE,"E0")}),-1.0]])]});
            extrude(context, id + "F1", {"entities" : qUnion([Q0]), "depth" : 76.2 * mm, "offsetDistance" : 25.4 * mm});
        }
        {
            var Q0;
            Q0=makeQuery(id+"F0.imprint","IMPRINT",FACE,{"disambiguationData":[TD([[makeQuery(id+"F0.imprint","IMPRINT",EDGE,{"derivedFrom":sQuery(id+"F0.wireOp",EDGE,"E181")}),-1.0]])]});
            var Q1;
            Q1=makeQuery(id+"F0.imprint","IMPRINT",FACE,{"disambiguationData":[TD([[makeQuery(id+"F0.imprint","IMPRINT",EDGE,{"derivedFrom":sQuery(id+"F0.wireOp",EDGE,"E194")}),-1.0]])]});
            var Q2;
            Q2=makeQuery(id+"F0.imprint","IMPRINT",FACE,{"disambiguationData":[TD([[makeQuery(id+"F0.imprint","IMPRINT",EDGE,{"derivedFrom":sQuery(id+"F0.wireOp",EDGE,"E213")}),-1.0]])]});
            var Q3;
            Q3=makeQuery(id+"F0.imprint","IMPRINT",FACE,{"disambiguationData":[TD([[makeQuery(id+"F0.imprint","IMPRINT",EDGE,{"derivedFrom":sQuery(id+"F0.wireOp",EDGE,"E229")}),1.0]])]});
            var Q4;
            Q4=makeQuery(id+"F0.imprint","IMPRINT",FACE,{"disambiguationData":[TD([[makeQuery(id+"F0.imprint","IMPRINT",EDGE,{"derivedFrom":sQuery(id+"F0.wireOp",EDGE,"E36")}),-1.0]])]});
            var Q5;
            Q5=makeQuery(id+"F0.imprint","IMPRINT",FACE,{"disambiguationData":[TD([[makeQuery(id+"F0.imprint","IMPRINT",EDGE,{"derivedFrom":sQuery(id+"F0.wireOp",EDGE,"E49")}),1.0]])]});
            var Q6;
            Q6=makeQuery(id+"F0.imprint","IMPRINT",FACE,{"disambiguationData":[TD([[makeQuery(id+"F0.imprint","IMPRINT",EDGE,{"derivedFrom":sQuery(id+"F0.wireOp",EDGE,"E60")}),1.0]])]});
            var Q7;
            Q7=makeQuery(id+"F0.imprint","IMPRINT",FACE,{"disambiguationData":[TD([[makeQuery(id+"F0.imprint","IMPRINT",EDGE,{"derivedFrom":sQuery(id+"F0.wireOp",EDGE,"E70")}),1.0]])]});
            var Q8;
            Q8=makeQuery(id+"F0.imprint","IMPRINT",FACE,{"disambiguationData":[TD([[makeQuery(id+"F0.imprint","IMPRINT",EDGE,{"derivedFrom":sQuery(id+"F0.wireOp",EDGE,"E80")}),1.0]])]});
            var Q9;
            Q9=makeQuery(id+"F0.imprint","IMPRINT",FACE,{"disambiguationData":[TD([[makeQuery(id+"F0.imprint","IMPRINT",EDGE,{"derivedFrom":sQuery(id+"F0.wireOp",EDGE,"E92")}),1.0]])]});
            var Q10;
            Q10=makeQuery(id+"F0.imprint","IMPRINT",FACE,{"disambiguationData":[TD([[makeQuery(id+"F0.imprint","IMPRINT",EDGE,{"derivedFrom":sQuery(id+"F0.wireOp",EDGE,"E114")}),1.0]])]});
            var Q11;
            Q11=makeQuery(id+"F0.imprint","IMPRINT",FACE,{"disambiguationData":[TD([[makeQuery(id+"F0.imprint","IMPRINT",EDGE,{"derivedFrom":sQuery(id+"F0.wireOp",EDGE,"E202")}),-1.0]])]});
            extrude(context, id + "F2", {"entities" : qUnion([Q0, Q1, Q2, Q3, Q4, Q5, Q6, Q7, Q8, Q9, Q10, Q11]), "depth" : 114.3 * mm, "offsetDistance" : 25.4 * mm});
        }
        {
            var Q0;
            Q0=makeQuery(id+"F0.imprint","IMPRINT",FACE,{"disambiguationData":[TD([[makeQuery(id+"F0.imprint","IMPRINT",EDGE,{"derivedFrom":sQuery(id+"F0.wireOp",EDGE,"E0")}),1.0]])]});
            var Q1;
            Q1=makeQuery(id+"F0.imprint","IMPRINT",FACE,{"disambiguationData":[TD([[makeQuery(id+"F0.imprint","IMPRINT",EDGE,{"derivedFrom":sQuery(id+"F0.wireOp",EDGE,"E28")}),-1.0]])]});
            var Q2;
            Q2=makeQuery(id+"F0.imprint","IMPRINT",FACE,{"disambiguationData":[TD([[makeQuery(id+"F0.imprint","IMPRINT",EDGE,{"derivedFrom":sQuery(id+"F0.wireOp",EDGE,"E32")}),1.0]])]});
            var Q3;
            Q3=makeQuery(id+"F0.imprint","IMPRINT",FACE,{"disambiguationData":[TD([[makeQuery(id+"F0.imprint","IMPRINT",EDGE,{"derivedFrom":sQuery(id+"F0.wireOp",EDGE,"E241")}),1.0]])]});
            var Q4;
            Q4=makeQuery(id+"F0.imprint","IMPRINT",FACE,{"disambiguationData":[TD([[makeQuery(id+"F0.imprint","IMPRINT",EDGE,{"derivedFrom":sQuery(id+"F0.wireOp",EDGE,"E141")}),1.0]])]});
            var Q5;
            Q5=makeQuery(id+"F0.imprint","IMPRINT",FACE,{"disambiguationData":[TD([[makeQuery(id+"F0.imprint","IMPRINT",EDGE,{"derivedFrom":sQuery(id+"F0.wireOp",EDGE,"E145")}),-1.0]])]});
            var Q6;
            Q6=makeQuery(id+"F0.imprint","IMPRINT",FACE,{"disambiguationData":[TD([[makeQuery(id+"F0.imprint","IMPRINT",EDGE,{"derivedFrom":sQuery(id+"F0.wireOp",EDGE,"E149")}),-1.0]])]});
            var Q7;
            Q7=makeQuery(id+"F0.imprint","IMPRINT",FACE,{"disambiguationData":[TD([[makeQuery(id+"F0.imprint","IMPRINT",EDGE,{"derivedFrom":sQuery(id+"F0.wireOp",EDGE,"E153")}),-1.0]])]});
            var Q8;
            Q8=makeQuery(id+"F0.imprint","IMPRINT",FACE,{"disambiguationData":[TD([[makeQuery(id+"F0.imprint","IMPRINT",EDGE,{"derivedFrom":sQuery(id+"F0.wireOp",EDGE,"E157")}),-1.0]])]});
            var Q9;
            Q9=makeQuery(id+"F0.imprint","IMPRINT",FACE,{"disambiguationData":[TD([[makeQuery(id+"F0.imprint","IMPRINT",EDGE,{"derivedFrom":sQuery(id+"F0.wireOp",EDGE,"E161")}),-1.0]])]});
            var Q10;
            Q10=makeQuery(id+"F0.imprint","IMPRINT",FACE,{"disambiguationData":[TD([[makeQuery(id+"F0.imprint","IMPRINT",EDGE,{"derivedFrom":sQuery(id+"F0.wireOp",EDGE,"E165")}),-1.0]])]});
            var Q11;
            Q11=makeQuery(id+"F0.imprint","IMPRINT",FACE,{"disambiguationData":[TD([[makeQuery(id+"F0.imprint","IMPRINT",EDGE,{"derivedFrom":sQuery(id+"F0.wireOp",EDGE,"E169")}),-1.0]])]});
            var Q12;
            Q12=makeQuery(id+"F0.imprint","IMPRINT",FACE,{"disambiguationData":[TD([[makeQuery(id+"F0.imprint","IMPRINT",EDGE,{"derivedFrom":sQuery(id+"F0.wireOp",EDGE,"E173")}),-1.0]])]});
            var Q13;
            Q13=makeQuery(id+"F0.imprint","IMPRINT",FACE,{"disambiguationData":[TD([[makeQuery(id+"F0.imprint","IMPRINT",EDGE,{"derivedFrom":sQuery(id+"F0.wireOp",EDGE,"E177")}),-1.0]])]});
            var Q14;
            Q14=makeQuery(id+"F0.imprint","IMPRINT",FACE,{"disambiguationData":[TD([[makeQuery(id+"F0.imprint","IMPRINT",EDGE,{"derivedFrom":sQuery(id+"F0.wireOp",EDGE,"E137")}),1.0]])]});
            extrude(context, id + "F3", {"entities" : qUnion([Q0, Q1, Q2, Q3, Q4, Q5, Q6, Q7, Q8, Q9, Q10, Q11, Q12, Q13, Q14]), "operationType" : NewBodyOperationType.ADD, "depth" : 114.3 * mm, "offsetDistance" : 25.4 * mm});
        }
        {
            var Q0;
            Q0=makeQuery(id+"F0.imprint","IMPRINT",FACE,{"disambiguationData":[TD([[makeQuery(id+"F0.imprint","IMPRINT",EDGE,{"derivedFrom":sQuery(id+"F0.wireOp",EDGE,"E269")}),1.0]])]});
            extrude(context, id + "F4", {"entities" : qUnion([Q0]), "operationType" : NewBodyOperationType.ADD, "depth" : 101.6 * mm, "offsetDistance" : 25.4 * mm});
        }
        {
            var Q0;
            Q0=makeQuery(id+"F0.imprint","IMPRINT",FACE,{"disambiguationData":[TD([[makeQuery(id+"F0.imprint","IMPRINT",EDGE,{"derivedFrom":sQuery(id+"F0.wireOp",EDGE,"E269")}),-1.0]])]});
            extrude(context, id + "F5", {"entities" : qUnion([Q0]), "operationType" : NewBodyOperationType.ADD, "depth" : 127 * mm, "offsetDistance" : 25.4 * mm});
        }
    });
